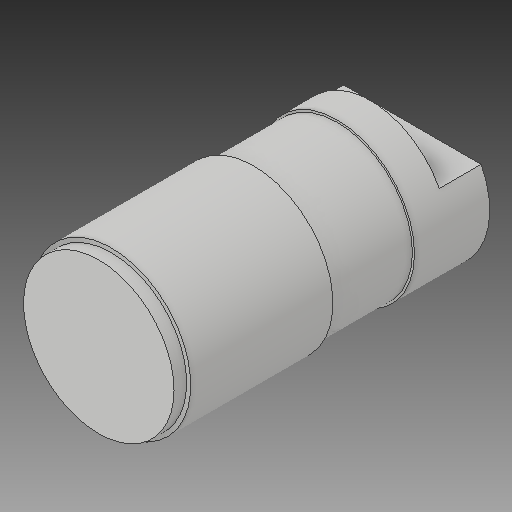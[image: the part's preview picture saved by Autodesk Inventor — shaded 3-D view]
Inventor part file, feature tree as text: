
AUTODESK INVENTOR PART (.ipt)
format: ipt  version: 2017 (Build 210142000, 142)  size: 641,024 bytes
history: native  units: in
note: dims shown in document units (in); Inventor stores cm internally (conversion verified against a paired STEP export)
features: extrude x1, sketch x1, other x1
ambient origin geometry x8: Origin, YZ Plane, XZ Plane, XY Plane, X Axis, Y Axis, Z Axis, Center Point
bodies: Solid1 (feature_tree)
feature tree (3):
  extrude  "Extrusion1"  [1 undecoded]
  sketch  "Sketch1"  dims[d0=2.3041in d1=0.0in]
  other  "Boss-Extrude10"
note: 1 required parameter value undecoded (feature->parameter linkage not recoverable at this tier; creation-order binding heuristic only, values carry confidence <= 0.55)
